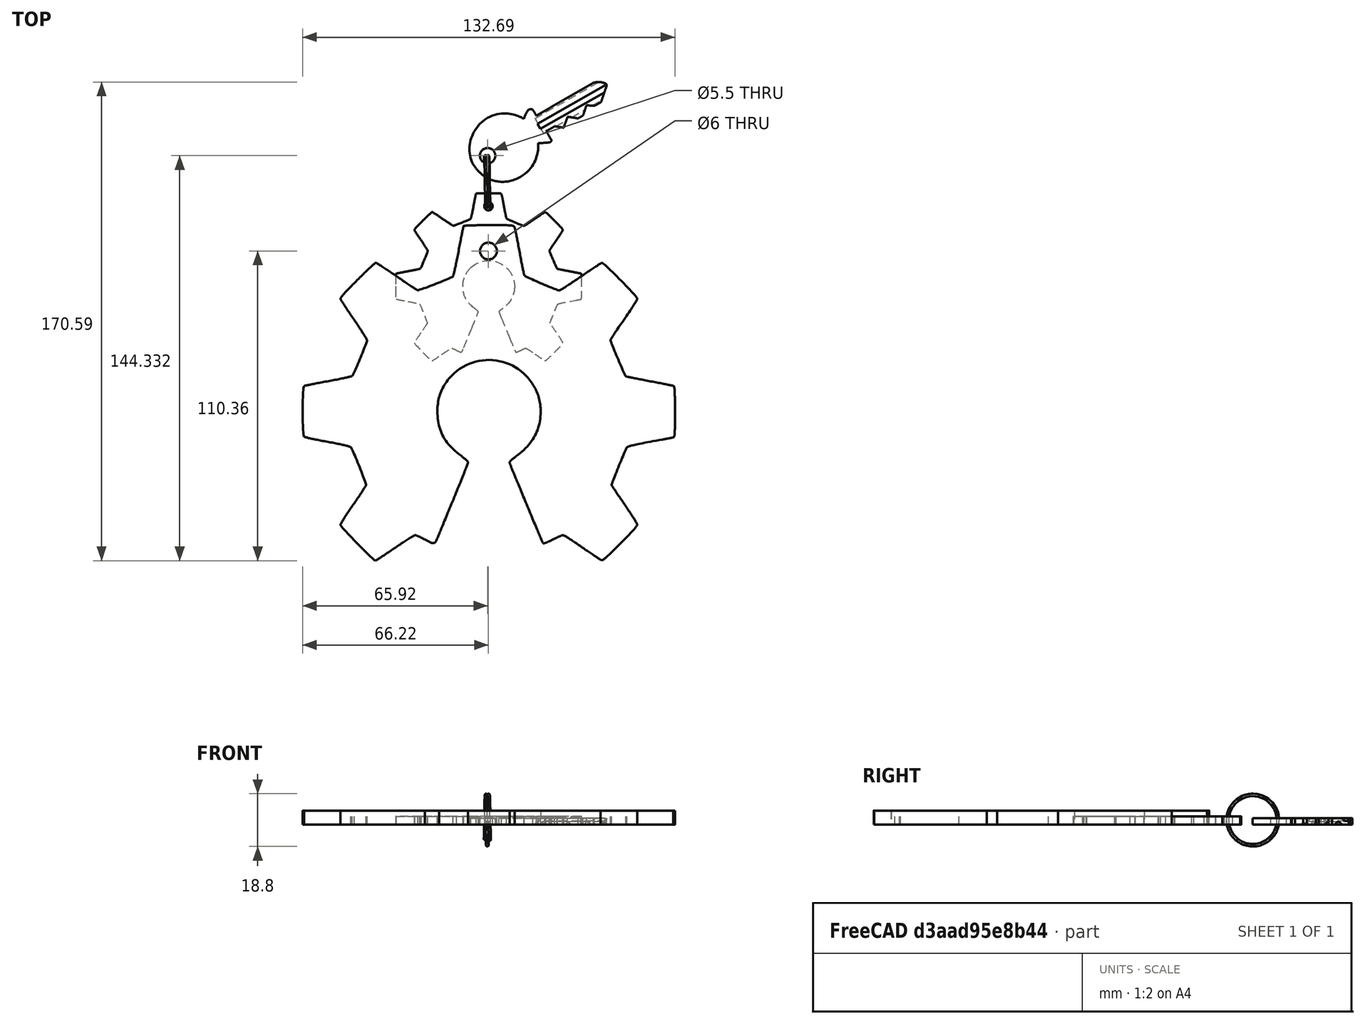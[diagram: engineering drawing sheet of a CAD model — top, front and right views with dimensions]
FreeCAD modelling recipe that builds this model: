
FCSTD DOCUMENT  (FreeCAD 0.15R4614 (Git))
Label: OpenHw
License: CC-BY 3.0
LicenseURL: http://creativecommons.org/licenses/by/3.0/
objects: Part::Feature×3, App::DocumentObjectGroup×2, Part::Extrusion×1, Part::Cylinder×1, Part::Cut×1, Part::FeaturePython×1
note: 7 computed .brp shape members not serialized (recipe doc carries the construction recipe); baked Part::Feature solids carry a one-line shape summary decoded from their .brp

FEATURE [Part::Feature] Path
  shape: bbox 132.9 x 119.6 x 2e-07 mm, 0 faces, 0 solids (baked)
FEATURE [Part::Extrusion] Extrude
  Base = -> Path
  Dir = (0,0,5)
  Placement = pos=(-69,-134,0) rot=(0,0,1;0rad)
  Solid = true
FEATURE [Part::Cylinder] Cylinder  label="Cilindro"
  Angle = 360
  Height = 10
  Placement = pos=(0,0,-1) rot=(0,0,1;0rad)
  Radius = 3
FEATURE [Part::Feature] Sweep  label="key-ring-model-1"
  Placement = pos=(-1.2,24.7546,1.6391) rot=(0.333333,0.881918,0.333333;1.69612rad)
  shape: bbox 3.31 x 27.02 x 26.33 mm, 4 faces (baked)
FEATURE [Part::Feature] Cut001  label="key-model-1"
  Placement = pos=(-5.46976,31.0266,0) rot=(0,0,1;0.517888rad)
  shape: bbox 49.82 x 36.6 x 2.3 mm, 44 faces (baked)
FEATURE [Part::Cut] Cut  label="LlaveroOriginal"
  Base = -> Extrude
  Tool = -> Cylinder
FEATURE [App::DocumentObjectGroup] Grupo001  label="OpenHw src"
  Group = -> [Cut]
FEATURE [Part::FeaturePython] Scale  label="openhw"  # WARN: FeaturePython — macro-defined, semantics opaque (R4)
  Placement = pos=(0,16,0) rot=(0,0,1;0rad)
  Scale = (0.5,0.5,0.6)
FEATURE [App::DocumentObjectGroup] Grupo  label="Assembly"
  Group = -> [Sweep,Cut001,Scale]
